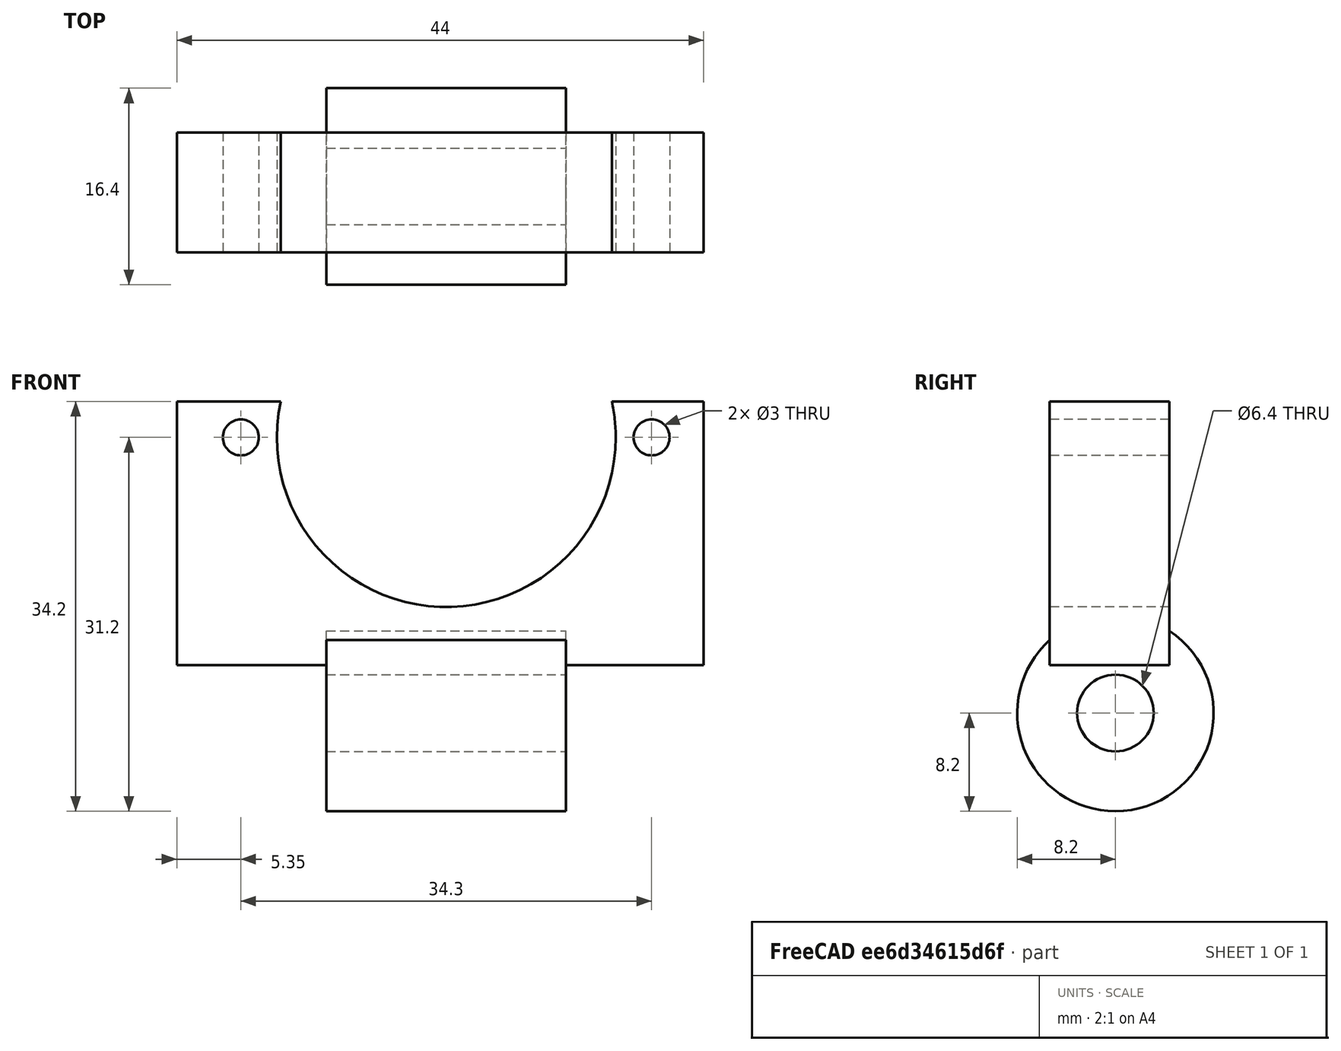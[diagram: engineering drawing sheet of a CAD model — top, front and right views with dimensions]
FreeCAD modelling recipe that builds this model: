
FCSTD DOCUMENT
Label: topOfStructure
objects: Part::Cylinder×4, Part::Cut×4, Part::MultiFuse×1
note: 9 computed .brp shape members not serialized (recipe doc carries the construction recipe); baked Part::Feature solids carry a one-line shape summary decoded from their .brp

FEATURE [Part::Cylinder] Cylinder001
  Angle = 360
  Height = 10
  Placement = pos=(5.35,23.5,19) rot=(1,0,0;1.5708rad)
  Radius = 1.5
FEATURE [Part::Cylinder] Cylinder001001
  Angle = 360
  Height = 10
  Placement = pos=(39.65,23.5,19) rot=(1,0,0;1.5708rad)
  Radius = 1.5
FEATURE [Part::Cut] Cut
FEATURE [Part::Cut] Cut001
  Base = -> Cut
  Tool = -> Cylinder001001
FEATURE [Part::Cut] Cut002001001
  Base = -> Cut001
  Placement = pos=(101,-19,0) rot=(0,0,1;0rad)
  Tool = -> Cylinder001
FEATURE [Part::Cylinder] Cylinder
  Angle = 360
  Height = 20
  Placement = pos=(113.5,0,-4) rot=(0,1,0;1.5708rad)
  Radius = 3.2
FEATURE [Part::Cylinder] Cylinder001002
  Angle = 360
  Height = 20
  Placement = pos=(113.5,0,-4) rot=(0,1,0;1.5708rad)
  Radius = 8.2
FEATURE [Part::Cut] Cut002001002
  Base = -> Cylinder001002
  Tool = -> Cylinder
FEATURE [Part::MultiFuse] Fusion
  Shapes = -> [Cut002001002,Cut002001001]
